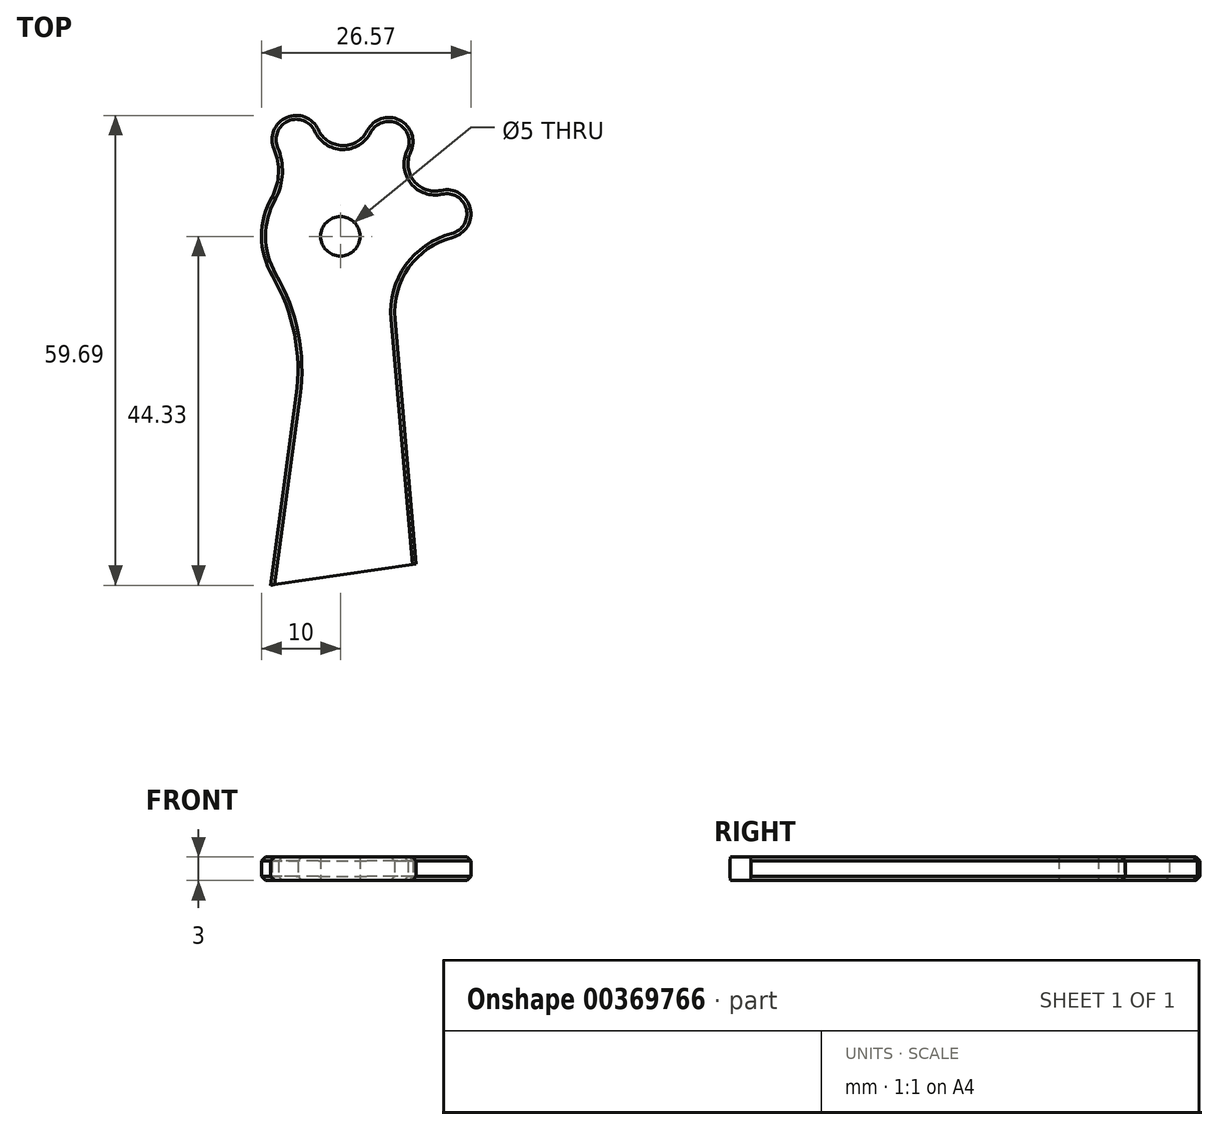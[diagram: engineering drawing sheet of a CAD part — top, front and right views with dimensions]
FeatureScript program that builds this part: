
annotation { "Feature Type Name" : "Feature", "Feature Type Description" : "" }
export const myFeature = defineFeature(function(context is Context, id is Id, definition is map)
    precondition{}
    {
        {
            var Q0;
            Q0=qCreatedBy(makeId("Top.planeOp"),FACE);
            var sketch = newSketch(context, id + "F0", { "sketchPlane" : qUnion([Q0])});
            skLineSegment(sketch, "E0", {"start": v(0, 22.23) * mm, "end": v(0, -19.2) * mm, "construction": true});
            skLineSegment(sketch, "E1", {"start": v(-19, 0) * mm, "end": v(18.86, 0) * mm, "construction": true});
            skCircle(sketch, "E2", {"center": v(0, 0) * mm, "radius": 6 * mm, "construction": true});
            skCircle(sketch, "E3", {"center": v(0, 0) * mm, "radius": 9 * mm, "construction": true});
            skLineSegment(sketch, "E4", {"start": v(-8.9, -44.33) * mm, "end": v(-5.6, -20.24) * mm});
            skCircle(sketch, "E5", {"center": v(0, 0) * mm, "radius": 10 * mm, "construction": true});
            skArc(sketch, "E6", {"start": v(-5.6, -20.24) * mm, "mid": v(-5.84, -12.39) * mm, "end": v(-8.63, -5.05) * mm});
            skArc(sketch, "E7", {"start": v(-8.63, -5.05) * mm, "mid": v(-9.83, -1.82) * mm, "end": v(-9.87, 1.63) * mm});
            skLineSegment(sketch, "E8", {"start": v(-7.92, 9.44) * mm, "end": v(0, 0) * mm, "construction": true});
            skLineSegment(sketch, "E9.anchor2", {"start": v(0, 0) * mm, "end": v(11.5, 7.82) * mm, "construction": true});
            skLineSegment(sketch, "E10", {"start": v(7.07, -7.07) * mm, "end": v(7.07, -7.07) * mm});
            skLineSegment(sketch, "E11", {"start": v(6.92, -10.5) * mm, "end": v(9.64, -41.63) * mm});
            skCircle(sketch, "E12", {"center": v(0, 0) * mm, "radius": 2.5 * mm});
            skLineSegment(sketch, "E13", {"start": v(-8.9, -44.33) * mm, "end": v(9.64, -41.63) * mm});
            skLineSegment(sketch, "E14", {"start": v(4.24, -4.24) * mm, "end": v(0, 0) * mm, "construction": true});
            skArc(sketch, "E15", {"start": v(12.8, 5.84) * mm, "mid": v(16.49, 3.57) * mm, "end": v(14.26, -0.14) * mm});
            skArc(sketch, "E16", {"start": v(14.26, -0.14) * mm, "mid": v(8.7, -3.97) * mm, "end": v(6.92, -10.5) * mm});
            skArc(sketch, "E17.1.0", {"start": v(3.41, 13.41) * mm, "mid": v(7.52, 14.77) * mm, "end": v(8.93, 10.69) * mm});
            skArc(sketch, "E17.2.0", {"start": v(-8.43, 11.08) * mm, "mid": v(-6.83, 15.1) * mm, "end": v(-2.8, 13.55) * mm});
            skPoint(sketch, "E17.center", {"position": v(-0.01, -0.45) * mm});
            skLineSegment(sketch, "E17.anchor1", {"start": v(-0.01, -0.45) * mm, "end": v(14.26, -0.14) * mm, "construction": true});
            skLineSegment(sketch, "E17.anchor2", {"start": v(-0.01, -0.45) * mm, "end": v(-2.8, 13.55) * mm, "construction": true});
            skArc(sketch, "E18", {"start": v(-2.8, 13.55) * mm, "mid": v(0.26, 11.53) * mm, "end": v(3.41, 13.41) * mm});
            skArc(sketch, "E19", {"start": v(8.93, 10.69) * mm, "mid": v(9.34, 7.04) * mm, "end": v(12.8, 5.84) * mm});
            skArc(sketch, "E20", {"start": v(-8.43, 11.08) * mm, "mid": v(-7.86, 8.02) * mm, "end": v(-8.65, 5.02) * mm});
            skArc(sketch, "E21", {"start": v(-9.87, 1.63) * mm, "mid": v(-9.41, 3.38) * mm, "end": v(-8.65, 5.02) * mm});
            skLineSegment(sketch, "E22", {"start": v(0, 0) * mm, "end": v(6.15, 12.02) * mm, "construction": true});
            skLineSegment(sketch, "E23", {"start": v(-80.22, 20.3) * mm, "end": v(-56.46, -13.63) * mm, "construction": true});
            skLineSegment(sketch, "E24", {"start": v(-83.03, -8.8) * mm, "end": v(-52.02, 12.9) * mm, "construction": true});
            skCircle(sketch, "E25", {"center": v(-66.54, 2.03) * mm, "radius": 6 * mm, "construction": true});
            skCircle(sketch, "E26", {"center": v(-66.54, 2.03) * mm, "radius": 9 * mm, "construction": true});
            skLineSegment(sketch, "E27", {"start": v(-78.45, 5.22) * mm, "end": v(-66.54, 2.03) * mm, "construction": true});
            skLineSegment(sketch, "E28.anchor2", {"start": v(-66.54, 2.03) * mm, "end": v(-61.6, 15.03) * mm, "construction": true});
            skLineSegment(sketch, "E29", {"start": v(-39.83, -20.57) * mm, "end": v(-39.83, -20.57) * mm});
            skCircle(sketch, "E30", {"center": v(-66.54, 2.03) * mm, "radius": 2.5 * mm, "construction": true});
            skLineSegment(sketch, "E31", {"start": v(-60.64, 0.98) * mm, "end": v(-66.54, 2.03) * mm, "construction": true});
            skArc(sketch, "E32", {"start": v(-57.8, 13.06) * mm, "mid": v(-53.5, 12.72) * mm, "end": v(-53.79, 8.4) * mm});
            skArc(sketch, "E33.1.0", {"start": v(-69.62, 15.52) * mm, "mid": v(-66.59, 18.6) * mm, "end": v(-63.47, 15.6) * mm});
            skArc(sketch, "E33.2.0", {"start": v(-79.1, 8.05) * mm, "mid": v(-79.5, 12.35) * mm, "end": v(-75.21, 12.82) * mm});
            skPoint(sketch, "E33.center", {"position": v(-66.35, 1.62) * mm});
            skArc(sketch, "E34", {"start": v(-75.21, 12.82) * mm, "mid": v(-71.56, 12.41) * mm, "end": v(-69.62, 15.52) * mm});
            skArc(sketch, "E35", {"start": v(-63.47, 15.6) * mm, "mid": v(-61.44, 12.55) * mm, "end": v(-57.8, 13.06) * mm});
            skLineSegment(sketch, "E36", {"start": v(-66.54, 2.03) * mm, "end": v(-66.54, 15.53) * mm, "construction": true});
            skLineSegment(sketch, "E37", {"start": v(-66.54, 2.03) * mm, "end": v(-66.54, -12.04) * mm, "construction": true});
            skArc(sketch, "E38", {"start": v(-79.1, 8.05) * mm, "mid": v(-73.04, 2.31) * mm, "end": v(-67.74, -4.14) * mm});
            skArc(sketch, "E39", {"start": v(-53.79, 8.4) * mm, "mid": v(-59.88, 2.43) * mm, "end": v(-65.32, -4.15) * mm});
            skPoint(sketch, "E40.visualSharp", {"position": v(-66.54, -5.85) * mm});
            skArc(sketch, "E40.filletArc", {"start": v(-67.74, -4.14) * mm, "mid": v(-66.53, -4.76) * mm, "end": v(-65.32, -4.15) * mm});
            skSolve(sketch);
        }
        {
            var Q0;
            Q0=makeQuery(id+"F0.imprint","IMPRINT",FACE,{"disambiguationData":[TD([[makeQuery(id+"F0.imprint","IMPRINT",EDGE,{"derivedFrom":sQuery(id+"F0.wireOp",EDGE,"E4")}),-1.0]])]});
            extrude(context, id + "F1", {"entities" : qUnion([Q0]), "depth" : 3 * mm});
        }
        {
            var Q0;
            Q0=makeQuery(id+"F1.opExtrude","CAP_EDGE",EDGE,{"disambiguationData":[OSD([sQuery(id+"F0.wireOp",EDGE,"E7"),sQuery(id+"F0.wireOp",EDGE,"E21")])],"isStart":true});
            var Q1;
            Q1=makeQuery(id+"F1.opExtrude","CAP_EDGE",EDGE,{"disambiguationData":[OSD([sQuery(id+"F0.wireOp",EDGE,"E17.2.0")])],"isStart":true});
            var Q2;
            Q2=makeQuery(id+"F1.opExtrude","CAP_EDGE",EDGE,{"disambiguationData":[OSD([sQuery(id+"F0.wireOp",EDGE,"E4")])],"isStart":false});
            var Q3;
            Q3=makeQuery(id+"F1.opExtrude","CAP_EDGE",EDGE,{"disambiguationData":[OSD([sQuery(id+"F0.wireOp",EDGE,"E18")])],"isStart":false});
            chamfer(context, id + "F2", {"entities" : qUnion([Q0, Q1, Q2, Q3]), "width" : .5 * mm, "tangentPropagation" : true});
        }
    });
